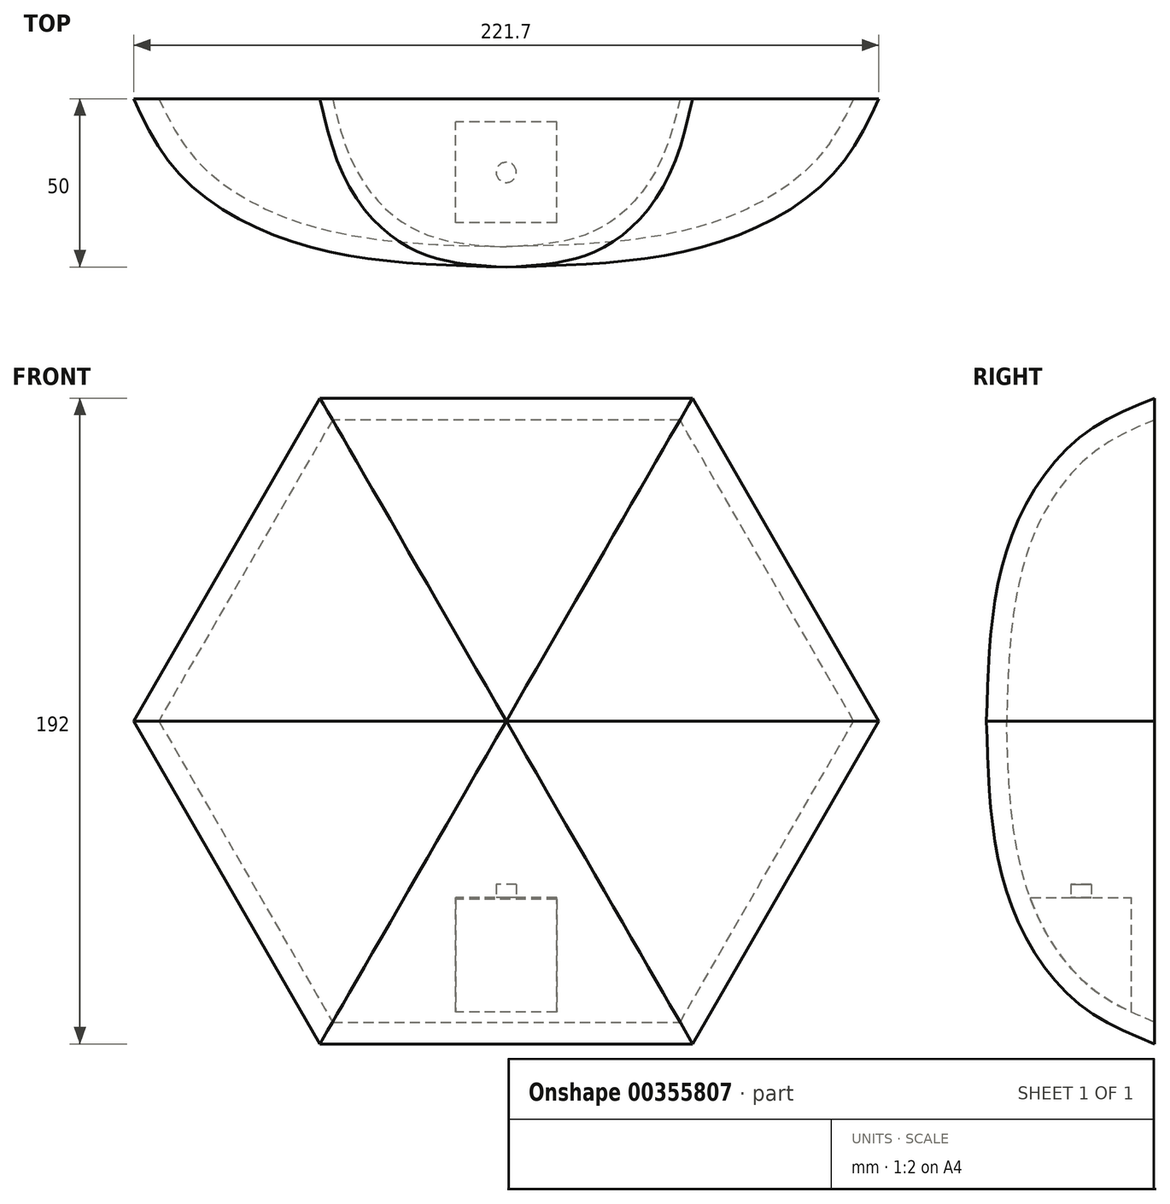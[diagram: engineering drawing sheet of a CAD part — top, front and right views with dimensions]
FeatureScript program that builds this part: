
annotation { "Feature Type Name" : "Feature", "Feature Type Description" : "" }
export const myFeature = defineFeature(function(context is Context, id is Id, definition is map)
    precondition{}
    {
        {
            var Q0;
            Q0=qCreatedBy(makeId("Front.planeOp"),FACE);
            var sketch = newSketch(context, id + "F0", { "sketchPlane" : qUnion([Q0])});
            skCircle(sketch, "E0.cCircle", {"center": v(0, 0) * mm, "radius": 96 * mm, "construction": true});
            skLineSegment(sketch, "E0.0", {"start": v(-55.43, 96) * mm, "end": v(55.43, 96) * mm});
            skLineSegment(sketch, "E0.1", {"start": v(55.43, 96) * mm, "end": v(110.85, 0) * mm});
            skLineSegment(sketch, "E0.2", {"start": v(110.85, 0) * mm, "end": v(55.43, -96) * mm});
            skLineSegment(sketch, "E0.3", {"start": v(55.43, -96) * mm, "end": v(-55.43, -96) * mm});
            skLineSegment(sketch, "E0.4", {"start": v(-55.43, -96) * mm, "end": v(-110.85, 0) * mm});
            skLineSegment(sketch, "E0.5", {"start": v(-110.85, 0) * mm, "end": v(-55.43, 96) * mm});
            skPoint(sketch, "E0.0.midPoint", {"position": v(0, 96) * mm});
            skSolve(sketch);
        }
        {
            var Q0;
            Q0=qCreatedBy(makeId("Front.planeOp"),FACE);
            cPlane(context, id + "F1", {"entities" : qUnion([Q0]), "cplaneType" : CPlaneType.OFFSET, "offset" : 20 * mm, "width" : 150 * mm, "height" : 150 * mm});
        }
        {
            var Q0;
            Q0=qCreatedBy(id+"F1.planeOp",FACE);
            var sketch = newSketch(context, id + "F2", { "sketchPlane" : qUnion([Q0])});
            skCircle(sketch, "E1.cCircle", {"center": v(0, 0) * mm, "radius": 86 * mm, "construction": true});
            skLineSegment(sketch, "E1.0", {"start": v(-49.65, 86) * mm, "end": v(49.65, 86) * mm});
            skLineSegment(sketch, "E1.1", {"start": v(49.65, 86) * mm, "end": v(99.3, 0) * mm});
            skLineSegment(sketch, "E1.2", {"start": v(99.3, 0) * mm, "end": v(49.65, -86) * mm});
            skLineSegment(sketch, "E1.3", {"start": v(49.65, -86) * mm, "end": v(-49.65, -86) * mm});
            skLineSegment(sketch, "E1.4", {"start": v(-49.65, -86) * mm, "end": v(-99.3, 0) * mm});
            skLineSegment(sketch, "E1.5", {"start": v(-99.3, 0) * mm, "end": v(-49.65, 86) * mm});
            skPoint(sketch, "E1.0.midPoint", {"position": v(0, 86) * mm});
            skSolve(sketch);
        }
        {
            var Q0;
            Q0=qCreatedBy(id+"F1.planeOp",FACE);
            cPlane(context, id + "F3", {"entities" : qUnion([Q0]), "cplaneType" : CPlaneType.OFFSET, "offset" : 20 * mm, "width" : 150 * mm, "height" : 150 * mm});
        }
        {
            var Q0;
            Q0=qCreatedBy(id+"F3.planeOp",FACE);
            var sketch = newSketch(context, id + "F4", { "sketchPlane" : qUnion([Q0])});
            skCircle(sketch, "E2.cCircle", {"center": v(0, 0) * mm, "radius": 61 * mm, "construction": true});
            skLineSegment(sketch, "E2.0", {"start": v(-35.22, 61) * mm, "end": v(35.22, 61) * mm});
            skLineSegment(sketch, "E2.1", {"start": v(35.22, 61) * mm, "end": v(70.44, 0) * mm});
            skLineSegment(sketch, "E2.2", {"start": v(70.44, 0) * mm, "end": v(35.22, -61) * mm});
            skLineSegment(sketch, "E2.3", {"start": v(35.22, -61) * mm, "end": v(-35.22, -61) * mm});
            skLineSegment(sketch, "E2.4", {"start": v(-35.22, -61) * mm, "end": v(-70.44, 0) * mm});
            skLineSegment(sketch, "E2.5", {"start": v(-70.44, 0) * mm, "end": v(-35.22, 61) * mm});
            skPoint(sketch, "E2.0.midPoint", {"position": v(0, 61) * mm});
            skSolve(sketch);
        }
        {
            var Q0;
            Q0=qCreatedBy(id+"F3.planeOp",FACE);
            cPlane(context, id + "F5", {"entities" : qUnion([Q0]), "cplaneType" : CPlaneType.OFFSET, "offset" : 10 * mm, "width" : 150 * mm, "height" : 150 * mm});
        }
        {
            var Q0;
            Q0=qCreatedBy(id+"F5.planeOp",FACE);
            var sketch = newSketch(context, id + "F6", { "sketchPlane" : qUnion([Q0])});
            skPoint(sketch, "E3", {"position": v(0, 0) * mm});
            skSolve(sketch);
        }
        {
            var Q0;
            Q0=makeQuery(id+"F0.imprint","IMPRINT",FACE,{"disambiguationData":[TD([[makeQuery(id+"F0.imprint","IMPRINT",EDGE,{"derivedFrom":sQuery(id+"F0.wireOp",EDGE,"E0.0")}),-1.0]])]});
            var Q1;
            Q1=makeQuery(id+"F2.imprint","IMPRINT",FACE,{"disambiguationData":[TD([[makeQuery(id+"F2.imprint","IMPRINT",EDGE,{"derivedFrom":sQuery(id+"F2.wireOp",EDGE,"E1.0")}),-1.0]])]});
            var Q2;
            Q2=makeQuery(id+"F4.imprint","IMPRINT",FACE,{"disambiguationData":[TD([[makeQuery(id+"F4.imprint","IMPRINT",EDGE,{"derivedFrom":sQuery(id+"F4.wireOp",EDGE,"E2.0")}),-1.0]])]});
            var Q3;
            Q3=sQuery(id+"F6.wireOp",VERTEX,"E3");
            loft(context, id + "F7", {"sheetProfilesArray" : [{ "sheetProfileEntities" : qUnion([Q0]) }, { "sheetProfileEntities" : qUnion([Q1]) }, { "sheetProfileEntities" : qUnion([Q2]) }, { "sheetProfileEntities" : qUnion([Q3]) }]});
        }
        {
            var Q0;
            Q0=makeQuery(id+"F7.opLoft","CAP_FACE",FACE,{"disambiguationData":[OSD([makeQuery(id+"F0.imprint","IMPRINT",FACE,{"disambiguationData":[TD([[makeQuery(id+"F0.imprint","IMPRINT",EDGE,{"derivedFrom":sQuery(id+"F0.wireOp",EDGE,"E0.0")}),-1.0]])]})])],"isStart":true});
            shell(context, id + "F8", {"entities" : qUnion([Q0]), "thickness" : 6 * mm});
        }
        {
            var Q0;
            Q0=qCreatedBy(makeId("Top.planeOp"),FACE);
            cPlane(context, id + "F9", {"entities" : qUnion([Q0]), "cplaneType" : CPlaneType.OFFSET, "offset" : 52.5 * mm, "oppositeDirection" : true, "width" : 150 * mm, "height" : 150 * mm});
        }
        {
            var Q0;
            Q0=qCreatedBy(id+"F9.planeOp",FACE);
            var sketch = newSketch(context, id + "F10", { "sketchPlane" : qUnion([Q0])});
            skLineSegment(sketch, "E4.bottom", {"start": v(15, -36.85) * mm, "end": v(-15, -36.85) * mm});
            skLineSegment(sketch, "E4.top", {"start": v(15, -6.85) * mm, "end": v(-15, -6.85) * mm});
            skLineSegment(sketch, "E4.left", {"start": v(15, -36.85) * mm, "end": v(15, -6.85) * mm});
            skLineSegment(sketch, "E4.right", {"start": v(-15, -36.85) * mm, "end": v(-15, -6.85) * mm});
            skPoint(sketch, "E4.middle", {"position": v(0, -21.85) * mm});
            skSolve(sketch);
        }
        {
            var Q0;
            Q0=qSketchRegion(id+"F10",true);
            extrude(context, id + "F11", {"entities" : qUnion([Q0]), "operationType" : NewBodyOperationType.ADD, "endBound" : BoundingType.UP_TO_NEXT, "oppositeDirection" : true, "depth" : 20 * mm});
        }
        {
            var Q0;
            Q0=makeQuery(id+"F11.opExtrude","CAP_FACE",FACE,{"disambiguationData":[OSD([sQuery(id+"F10.wireOp",EDGE,"E4.bottom"),sQuery(id+"F10.wireOp",EDGE,"E4.top"),sQuery(id+"F10.wireOp",EDGE,"E4.left"),sQuery(id+"F10.wireOp",EDGE,"E4.right")])],"isStart":true});
            var sketch = newSketch(context, id + "F12", { "sketchPlane" : qUnion([Q0])});
            skCircle(sketch, "E5", {"center": v(0, -21.85) * mm, "radius": 3 * mm});
            skPoint(sketch, "E5.centerSnap0", {"position": v(15, -21.85) * mm});
            skSolve(sketch);
        }
        {
            var Q0;
            Q0=qSketchRegion(id+"F12",true);
            extrude(context, id + "F13", {"entities" : qUnion([Q0]), "operationType" : NewBodyOperationType.ADD, "depth" : 4 * mm});
        }
    });
